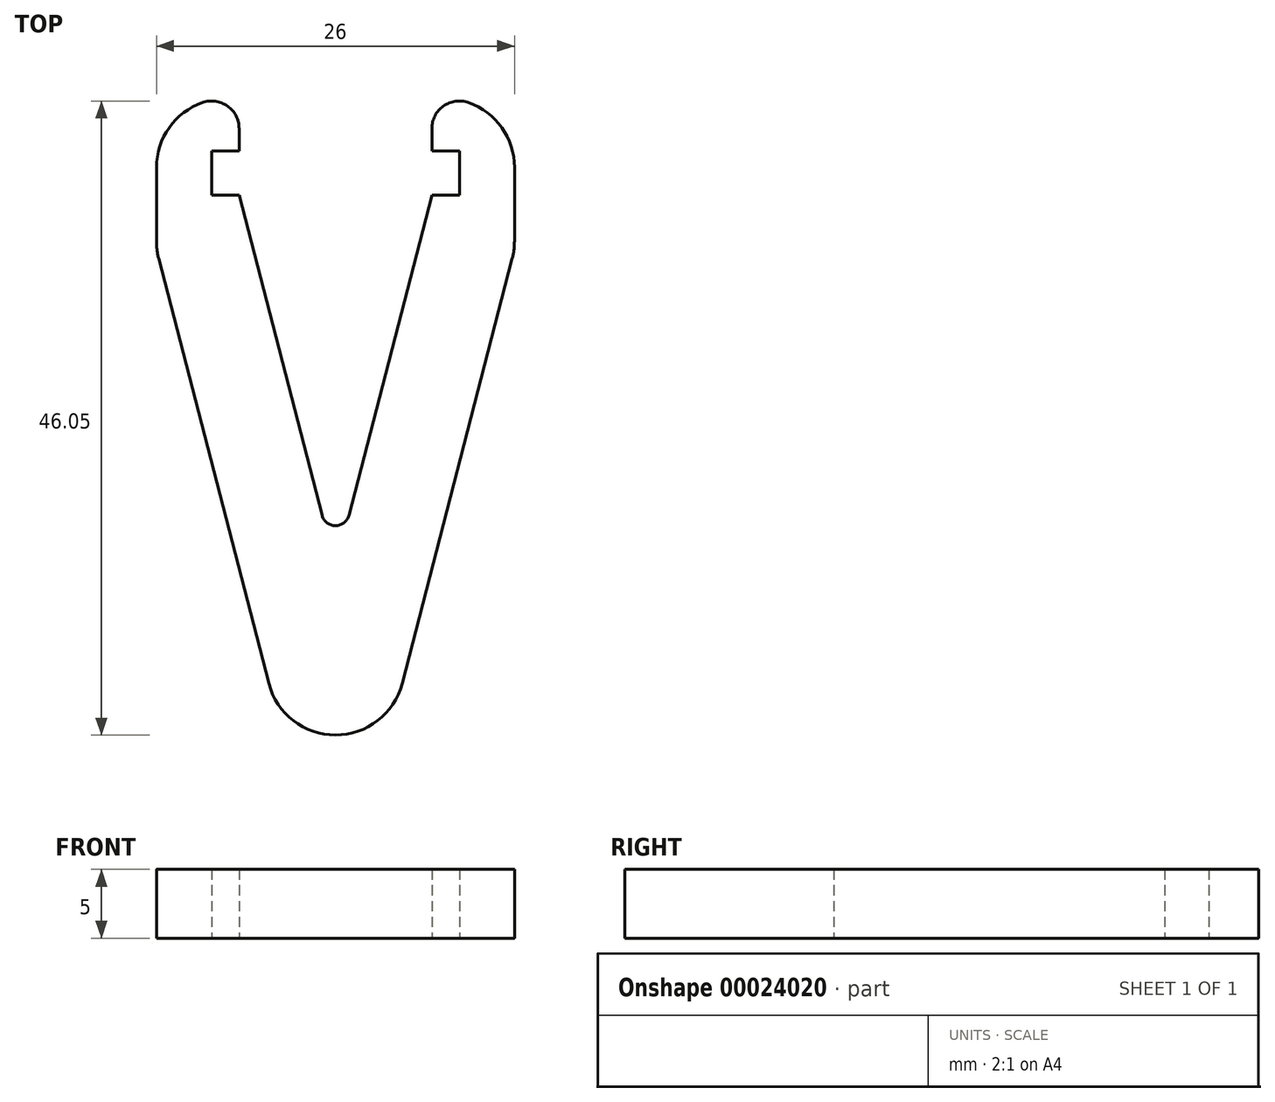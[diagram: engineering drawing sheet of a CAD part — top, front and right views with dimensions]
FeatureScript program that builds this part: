
annotation { "Feature Type Name" : "Feature", "Feature Type Description" : "" }
export const myFeature = defineFeature(function(context is Context, id is Id, definition is map)
    precondition{}
    {
        {
            var Q0;
            Q0=qCreatedBy(makeId("Top.planeOp"),FACE);
            var sketch = newSketch(context, id + "F0", { "sketchPlane" : qUnion([Q0])});
            skLineSegment(sketch, "E0.rect.bottom", {"start": v(9, -1.6) * mm, "end": v(-9, -1.6) * mm});
            skLineSegment(sketch, "E0.rect.top", {"start": v(9, 1.6) * mm, "end": v(-9, 1.6) * mm});
            skLineSegment(sketch, "E0.rect.left", {"start": v(9, -1.6) * mm, "end": v(9, 1.6) * mm});
            skLineSegment(sketch, "E0.rect.right", {"start": v(-9, -1.6) * mm, "end": v(-9, 1.6) * mm});
            skPoint(sketch, "E0.rect.middle", {"position": v(0, 0) * mm});
            skLineSegment(sketch, "E1", {"start": v(0, -1.6) * mm, "end": v(0, -28.6) * mm, "construction": true});
            skLineSegment(sketch, "E2", {"start": v(0, -1.6) * mm, "end": v(-7, -1.6) * mm});
            skLineSegment(sketch, "E3", {"start": v(0, 0) * mm, "end": v(0, 8.22) * mm, "construction": true});
            skLineSegment(sketch, "E4", {"start": v(0, 0) * mm, "end": v(-18.96, 0) * mm, "construction": true});
            skLineSegment(sketch, "E5.MirrorCS", {"start": v(0, 1.6) * mm, "end": v(-7, 1.6) * mm});
            skLineSegment(sketch, "E6", {"start": v(-7, 1.6) * mm, "end": v(-7, 5.4) * mm});
            skLineSegment(sketch, "E7", {"start": v(-7, -1.6) * mm, "end": v(0, -28.6) * mm});
            skLineSegment(sketch, "E8", {"start": v(-7, 5.4) * mm, "end": v(-13, 5.4) * mm});
            skLineSegment(sketch, "E9", {"start": v(-13, 5.4) * mm, "end": v(-13, -5.6) * mm});
            skLineSegment(sketch, "E10", {"start": v(-13, -5.6) * mm, "end": v(0, -55.74) * mm});
            skLineSegment(sketch, "E11", {"start": v(0, -28.6) * mm, "end": v(0, -98.8) * mm, "construction": true});
            skLineSegment(sketch, "E12.MirrorCS", {"start": v(7, -1.6) * mm, "end": v(0, -28.6) * mm});
            skLineSegment(sketch, "E13.MirrorCS", {"start": v(7, 5.4) * mm, "end": v(13, 5.4) * mm});
            skLineSegment(sketch, "E14.MirrorCS", {"start": v(7, 1.6) * mm, "end": v(7, 5.4) * mm});
            skLineSegment(sketch, "E15.MirrorCS", {"start": v(13, 5.4) * mm, "end": v(13, -5.6) * mm});
            skLineSegment(sketch, "E16.MirrorCS", {"start": v(13, -5.6) * mm, "end": v(0, -55.74) * mm});
            skSolve(sketch);
        }
        {
            var Q0;
            {var subQ4=sQuery(id+"F0.wireOp",EDGE,"E0.rect.left");Q0=makeQuery(id+"F0.imprint","IMPRINT",FACE,{"disambiguationData":[TD([[makeQuery(id+"F0.imprint","IMPRINT",EDGE,{"derivedFrom":subQ4}),-1.0]])]});}
            extrude(context, id + "F1", {"entities" : qUnion([Q0]), "depth" : 5 * mm});
        }
        {
            var Q0;
            Q0=makeQuery(id+"F1.opExtrude","SWEPT_EDGE",EDGE,{"disambiguationData":[OSD([sQuery(id+"F0.wireOp",EDGE,"E10"),sQuery(id+"F0.wireOp",EDGE,"E16.MirrorCS")])]});
            fillet(context, id + "F2", {"entities" : qUnion([Q0]), "radius" : 5 * mm, "tangentPropagation" : true, "allowEdgeOverflow" : false});
        }
        {
            var Q0;
            Q0=makeQuery(id+"F1.opExtrude","SWEPT_EDGE",EDGE,{"disambiguationData":[OSD([sQuery(id+"F0.wireOp",EDGE,"E9"),sQuery(id+"F0.wireOp",EDGE,"E10")])]});
            var Q1;
            Q1=makeQuery(id+"F1.opExtrude","SWEPT_EDGE",EDGE,{"disambiguationData":[OSD([sQuery(id+"F0.wireOp",EDGE,"E8"),sQuery(id+"F0.wireOp",EDGE,"E9")])]});
            var Q2;
            Q2=makeQuery(id+"F1.opExtrude","SWEPT_EDGE",EDGE,{"disambiguationData":[OSD([sQuery(id+"F0.wireOp",EDGE,"E13.MirrorCS"),sQuery(id+"F0.wireOp",EDGE,"E15.MirrorCS")])]});
            var Q3;
            Q3=makeQuery(id+"F1.opExtrude","SWEPT_EDGE",EDGE,{"disambiguationData":[OSD([sQuery(id+"F0.wireOp",EDGE,"E15.MirrorCS"),sQuery(id+"F0.wireOp",EDGE,"E16.MirrorCS")])]});
            fillet(context, id + "F3", {"entities" : qUnion([Q0, Q1, Q2, Q3]), "radius" : 5 * mm, "tangentPropagation" : true, "allowEdgeOverflow" : false});
        }
        {
            var Q0;
            Q0=makeQuery(id+"F1.opExtrude","SWEPT_EDGE",EDGE,{"disambiguationData":[OSD([sQuery(id+"F0.wireOp",EDGE,"E6"),sQuery(id+"F0.wireOp",EDGE,"E8")])]});
            var Q1;
            Q1=makeQuery(id+"F1.opExtrude","SWEPT_EDGE",EDGE,{"disambiguationData":[OSD([sQuery(id+"F0.wireOp",EDGE,"E13.MirrorCS"),sQuery(id+"F0.wireOp",EDGE,"E14.MirrorCS")])]});
            fillet(context, id + "F4", {"entities" : qUnion([Q0, Q1]), "radius" : 2 * mm, "tangentPropagation" : true, "allowEdgeOverflow" : false});
        }
        {
            var Q0;
            Q0=makeQuery(id+"F1.opExtrude","SWEPT_EDGE",EDGE,{"disambiguationData":[OSD([sQuery(id+"F0.wireOp",EDGE,"E7"),sQuery(id+"F0.wireOp",EDGE,"E12.MirrorCS")])]});
            fillet(context, id + "F5", {"entities" : qUnion([Q0]), "radius" : 1 * mm, "tangentPropagation" : true, "allowEdgeOverflow" : false});
        }
    });
